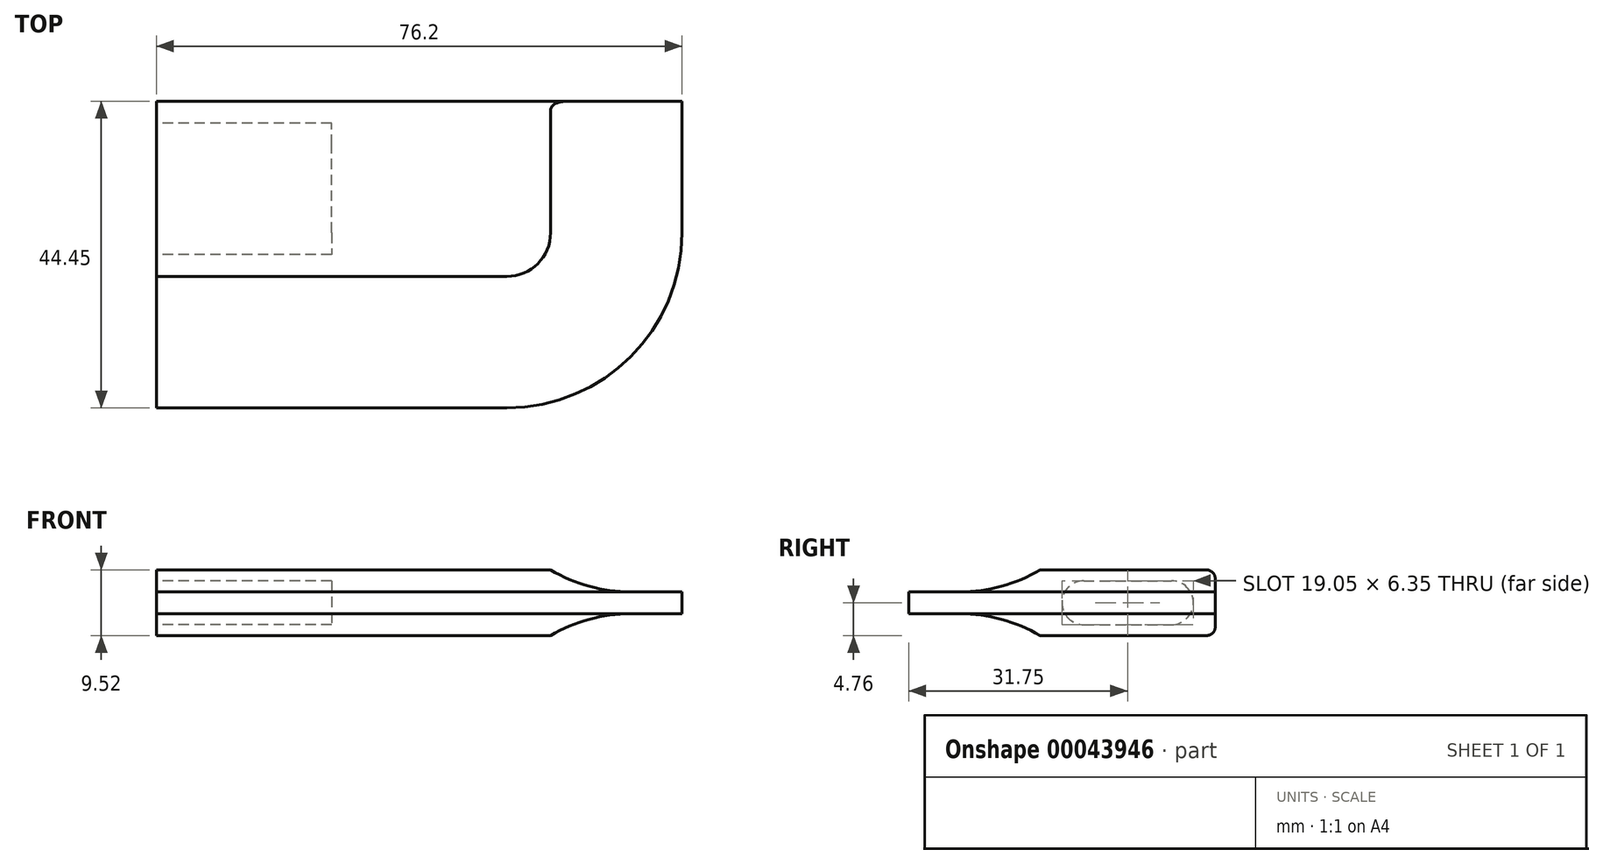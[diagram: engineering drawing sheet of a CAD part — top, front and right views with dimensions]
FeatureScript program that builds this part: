
annotation { "Feature Type Name" : "Feature", "Feature Type Description" : "" }
export const myFeature = defineFeature(function(context is Context, id is Id, definition is map)
    precondition{}
    {
        {
            var Q0;
            Q0=qCreatedBy(makeId("Top.planeOp"),FACE);
            var sketch = newSketch(context, id + "F0", { "sketchPlane" : qUnion([Q0])});
            skLineSegment(sketch, "E0", {"start": v(0, 0) * mm, "end": v(0, 44.45) * mm});
            skLineSegment(sketch, "E1", {"start": v(0, 44.45) * mm, "end": v(76.2, 44.45) * mm});
            skLineSegment(sketch, "E2", {"start": v(76.2, 44.45) * mm, "end": v(76.2, 25.4) * mm});
            skArc(sketch, "E3", {"start": v(76.2, 25.4) * mm, "mid": v(68.76, 7.44) * mm, "end": v(50.8, 0) * mm});
            skLineSegment(sketch, "E4", {"start": v(0, 0) * mm, "end": v(50.8, 0) * mm});
            skSolve(sketch);
        }
        {
            var Q0;
            Q0 = qSketchRegion(id + "F0", true);
            extrude(context, id + "F1", {"entities" : qUnion([Q0]), "endBound" : BoundingType.SYMMETRIC, "depth" : 9.52 * mm});
        }
        {
            var Q0;
            Q0=makeQuery(id+"F1.opExtrude","SWEPT_FACE",FACE,{"disambiguationData":[OSD([sQuery(id+"F0.wireOp",EDGE,"E0")])]});
            var sketch = newSketch(context, id + "F2", { "sketchPlane" : qUnion([Q0])});
            skArc(sketch, "E5", {"start": v(-19.05, 4.76) * mm, "mid": v(-13.45, 2.4) * mm, "end": v(-7.43, 1.59) * mm});
            skLineSegment(sketch, "E6", {"start": v(-7.43, 1.59) * mm, "end": v(0, 1.59) * mm});
            skLineSegment(sketch, "E7", {"start": v(0, 1.59) * mm, "end": v(0, 4.76) * mm});
            skLineSegment(sketch, "E8", {"start": v(0, 4.76) * mm, "end": v(-19.05, 4.76) * mm});
            skSolve(sketch);
        }
        {
            var Q0;
            Q0=makeQuery(id+"F1.opExtrude","CAP_FACE",FACE,{"disambiguationData":[OSD([sQuery(id+"F0.wireOp",EDGE,"E0"),sQuery(id+"F0.wireOp",EDGE,"E1"),sQuery(id+"F0.wireOp",EDGE,"E2"),sQuery(id+"F0.wireOp",EDGE,"E3"),sQuery(id+"F0.wireOp",EDGE,"E4")])],"isStart":false});
            var sketch = newSketch(context, id + "F3", { "sketchPlane" : qUnion([Q0])});
            skLineSegment(sketch, "E9", {"start": v(0, 0) * mm, "end": v(50.8, 0) * mm});
            skLineSegment(sketch, "E10", {"start": v(76.2, 44.45) * mm, "end": v(76.2, 25.4) * mm});
            skArc(sketch, "E11", {"start": v(76.2, 25.4) * mm, "mid": v(68.76, 7.44) * mm, "end": v(50.8, 0) * mm});
            skSolve(sketch);
        }
        {
            var Q0;
            Q0=makeQuery(id+"F2.imprint","IMPRINT",FACE,{"disambiguationData":[TD([[makeQuery(id+"F2.imprint","IMPRINT",EDGE,{"derivedFrom":sQuery(id+"F2.wireOp",EDGE,"E5")}),1.0]])]});
            var Q1;
            Q1=sQuery(id+"F3.wireOp",EDGE,"E9");
            var Q2;
            Q2=sQuery(id+"F3.wireOp",EDGE,"E11");
            var Q3;
            Q3=sQuery(id+"F3.wireOp",EDGE,"E10");
            sweep(context, id + "F4", {"profiles" : qUnion([Q0]), "path" : qUnion([Q1, Q2, Q3])});
        }
        {
            var Q0;
            Q0=makeQuery(id+"F4.opSweep","SWEPT_BODY",BODY,{"disambiguationData":[OSD([sQuery(id+"F2.wireOp",EDGE,"E5"),sQuery(id+"F2.wireOp",EDGE,"E6"),sQuery(id+"F2.wireOp",EDGE,"E7"),sQuery(id+"F2.wireOp",EDGE,"E8"),sQuery(id+"F3.wireOp",EDGE,"E10")])]});
            var Q1;
            Q1=makeQuery(id+"F4.boolean.opBoolean","COPY",FACE,{"derivedFrom":makeQuery(id+"F4.opSweep","SWEPT_FACE",FACE,{"disambiguationData":[OSD([sQuery(id+"F2.wireOp",EDGE,"E5"),sQuery(id+"F3.wireOp",EDGE,"E9")])]})});
            var Q2;
            Q2=makeQuery(id+"F4.boolean.opBoolean","COPY",FACE,{"derivedFrom":makeQuery(id+"F4.opSweep","SWEPT_FACE",FACE,{"disambiguationData":[OSD([sQuery(id+"F2.wireOp",EDGE,"E5"),sQuery(id+"F3.wireOp",EDGE,"E11")])]})});
            var Q3;
            Q3=makeQuery(id+"F4.boolean.opBoolean","COPY",FACE,{"derivedFrom":makeQuery(id+"F4.opSweep","SWEPT_FACE",FACE,{"disambiguationData":[OSD([sQuery(id+"F2.wireOp",EDGE,"E5"),sQuery(id+"F3.wireOp",EDGE,"E10")])]})});
            var Q4;
            Q4=makeQuery(id+"F4.boolean.opBoolean","COPY",FACE,{"derivedFrom":makeQuery(id+"F4.opSweep","SWEPT_FACE",FACE,{"disambiguationData":[OSD([sQuery(id+"F2.wireOp",EDGE,"E6"),sQuery(id+"F3.wireOp",EDGE,"E9")])]})});
            var Q5;
            Q5=qCreatedBy(makeId("Top.planeOp"),FACE);
            mirror(context, id + "F5", {"entities" : qUnion([Q0]), "faces" : qUnion([Q1, Q2, Q3, Q4]), "mirrorPlane" : qUnion([Q5])});
        }
        {
            var Q0;
            Q0=makeQuery(id+"F4.opSweep","SWEPT_BODY",BODY,{"disambiguationData":[OSD([sQuery(id+"F2.wireOp",EDGE,"E5"),sQuery(id+"F2.wireOp",EDGE,"E6"),sQuery(id+"F2.wireOp",EDGE,"E7"),sQuery(id+"F2.wireOp",EDGE,"E8"),sQuery(id+"F3.wireOp",EDGE,"E10")])]});
            var Q1;
            Q1=makeQuery(id+"F5.opPattern","COPY",BODY,{"derivedFrom":makeQuery(id+"F4.opSweep","SWEPT_BODY",BODY,{"disambiguationData":[OSD([sQuery(id+"F2.wireOp",EDGE,"E5"),sQuery(id+"F2.wireOp",EDGE,"E6"),sQuery(id+"F2.wireOp",EDGE,"E7"),sQuery(id+"F2.wireOp",EDGE,"E8"),sQuery(id+"F3.wireOp",EDGE,"E10")])]}),"instanceName":"1"});
            var Q2;
            Q2=makeQuery(id+"F1.opExtrude","SWEPT_BODY",BODY,{"disambiguationData":[OSD([sQuery(id+"F0.wireOp",EDGE,"E0"),sQuery(id+"F0.wireOp",EDGE,"E1"),sQuery(id+"F0.wireOp",EDGE,"E2"),sQuery(id+"F0.wireOp",EDGE,"E3"),sQuery(id+"F0.wireOp",EDGE,"E4")])]});
            booleanBodies(context, id + "F6", {"operationType" : BooleanOperationType.SUBTRACTION, "tools" : qUnion([Q0, Q1]), "targets" : qUnion([Q2])});
        }
        {
            var Q0;
            Q0=makeQuery(id+"F1.opExtrude","SWEPT_FACE",FACE,{"disambiguationData":[OSD([sQuery(id+"F0.wireOp",EDGE,"E0")])]});
            var sketch = newSketch(context, id + "F7", { "sketchPlane" : qUnion([Q0])});
            skLineSegment(sketch, "E12.rect.bottom", {"start": v(-25.4, -3.18) * mm, "end": v(-38.1, -3.17) * mm});
            skLineSegment(sketch, "E12.rect.top", {"start": v(-25.4, 3.17) * mm, "end": v(-38.1, 3.18) * mm});
            skLineSegment(sketch, "E12.rect.left", {"start": v(-22.23, 0) * mm, "end": v(-22.23, 0) * mm});
            skLineSegment(sketch, "E12.rect.right", {"start": v(-41.28, 0) * mm, "end": v(-41.28, 0) * mm});
            skPoint(sketch, "E12.rect.middle", {"position": v(-31.75, 0) * mm});
            skPoint(sketch, "E13.visualSharp", {"position": v(-41.28, -3.17) * mm});
            skArc(sketch, "E13.filletArc", {"start": v(-41.28, 0) * mm, "mid": v(-40.35, -2.25) * mm, "end": v(-38.1, -3.17) * mm});
            skPoint(sketch, "E14.visualSharp", {"position": v(-41.28, 3.18) * mm});
            skArc(sketch, "E14.filletArc", {"start": v(-38.1, 3.18) * mm, "mid": v(-40.35, 2.25) * mm, "end": v(-41.28, 0) * mm});
            skPoint(sketch, "E15.visualSharp", {"position": v(-22.23, 3.18) * mm});
            skArc(sketch, "E15.filletArc", {"start": v(-22.23, 0) * mm, "mid": v(-23.15, 2.25) * mm, "end": v(-25.4, 3.18) * mm});
            skPoint(sketch, "E16.visualSharp", {"position": v(-22.23, -3.18) * mm});
            skArc(sketch, "E16.filletArc", {"start": v(-25.4, -3.17) * mm, "mid": v(-23.15, -2.25) * mm, "end": v(-22.23, 0) * mm});
            skLineSegment(sketch, "E17", {"start": v(-44.45, 4.76) * mm, "end": v(-19.05, -4.76) * mm, "construction": true});
            skLineSegment(sketch, "E18", {"start": v(-19.05, 4.76) * mm, "end": v(-44.45, -4.76) * mm, "construction": true});
            skSolve(sketch);
        }
        {
            var Q0;
            Q0 = qSketchRegion(id + "F7", true);
            extrude(context, id + "F8", {"entities" : qUnion([Q0]), "operationType" : NewBodyOperationType.REMOVE, "oppositeDirection" : true, "depth" : 25.4 * mm});
        }
        {
            var Q0;
            Q0=makeQuery(id+"F6.opBoolean","COPY",EDGE,{"derivedFrom":makeQuery(id+"F4.opSweep","SWEPT_EDGE",EDGE,{"disambiguationData":[OSD([sQuery(id+"F0.wireOp",EDGE,"E0"),sQuery(id+"F0.wireOp",EDGE,"E4"),sQuery(id+"F2.wireOp",EDGE,"E6"),sQuery(id+"F2.wireOp",EDGE,"E7"),sQuery(id+"F3.wireOp",EDGE,"E9")])]})});
            var Q1;
            Q1=makeQuery(id+"F6.opBoolean","COPY",EDGE,{"derivedFrom":makeQuery(id+"F5.opPattern","COPY",EDGE,{"derivedFrom":makeQuery(id+"F4.opSweep","SWEPT_EDGE",EDGE,{"disambiguationData":[OSD([sQuery(id+"F0.wireOp",EDGE,"E0"),sQuery(id+"F0.wireOp",EDGE,"E4"),sQuery(id+"F2.wireOp",EDGE,"E6"),sQuery(id+"F2.wireOp",EDGE,"E7"),sQuery(id+"F3.wireOp",EDGE,"E9")])]}),"instanceName":"1"})});
            var Q2;
            Q2=makeQuery(id+"F1.opExtrude","CAP_EDGE",EDGE,{"disambiguationData":[OSD([sQuery(id+"F0.wireOp",EDGE,"E1")])],"isStart":false});
            var Q3;
            Q3=makeQuery(id+"F1.opExtrude","CAP_EDGE",EDGE,{"disambiguationData":[OSD([sQuery(id+"F0.wireOp",EDGE,"E1")])],"isStart":true});
            fillet(context, id + "F9", {"entities" : qUnion([Q0, Q1, Q2, Q3]), "radius" : 1.27 * mm, "tangentPropagation" : true, "allowEdgeOverflow" : false});
        }
    });
